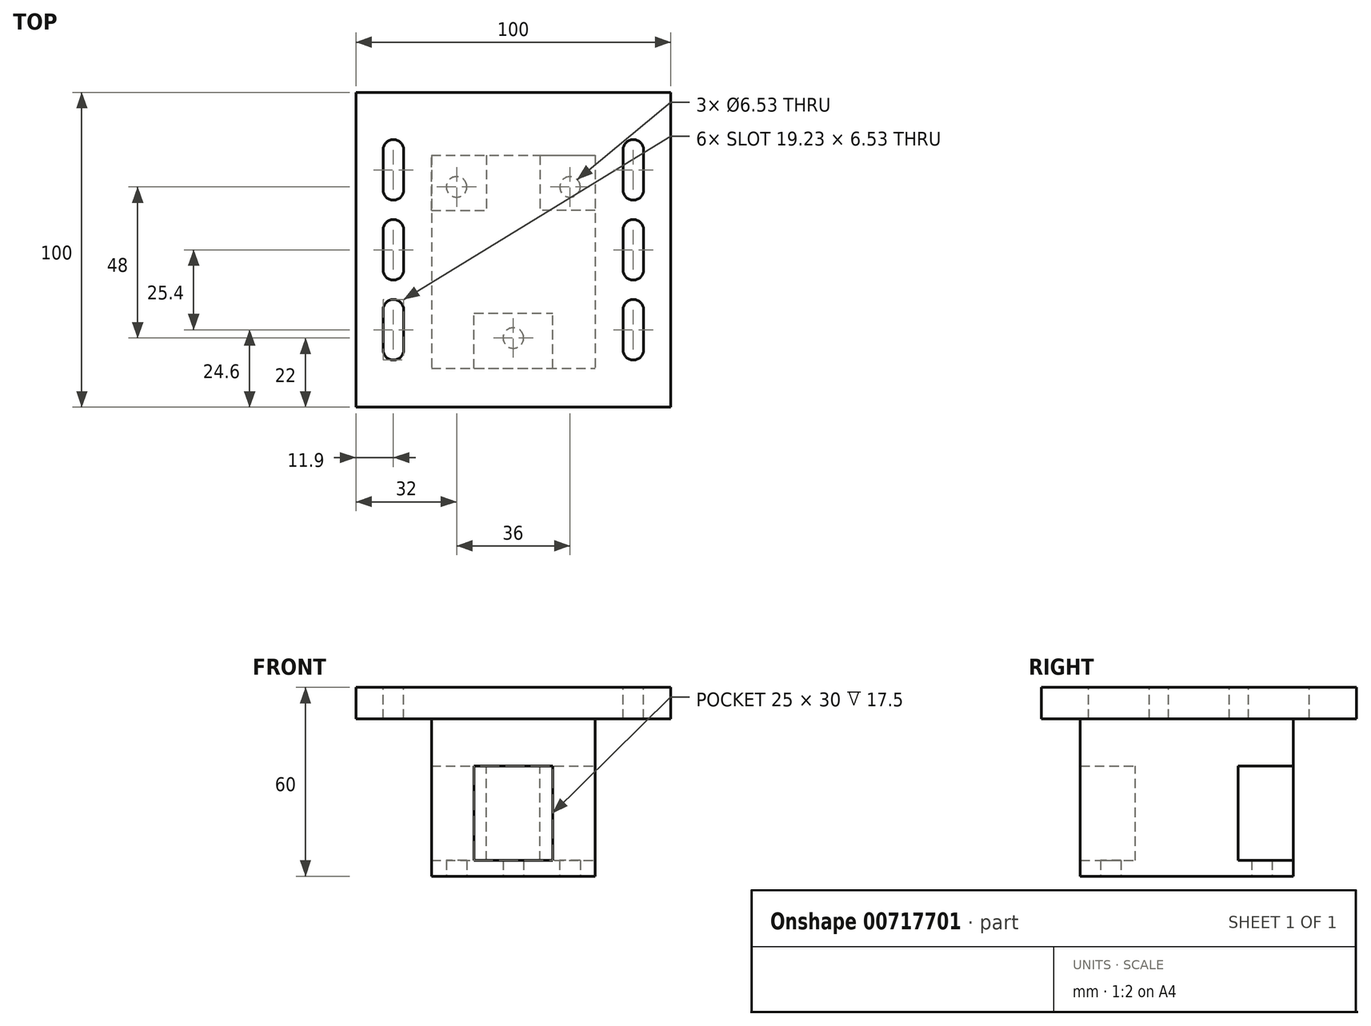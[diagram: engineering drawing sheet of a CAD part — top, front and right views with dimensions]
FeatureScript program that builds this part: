
annotation { "Feature Type Name" : "Feature", "Feature Type Description" : "" }
export const myFeature = defineFeature(function(context is Context, id is Id, definition is map)
    precondition{}
    {
        {
            var Q0;
            Q0=qCreatedBy(makeId("Top.planeOp"),FACE);
            var sketch = newSketch(context, id + "F0", { "sketchPlane" : qUnion([Q0])});
            skLineSegment(sketch, "E0.bottom", {"start": v(-26, 30) * mm, "end": v(26, 30) * mm});
            skLineSegment(sketch, "E0.top", {"start": v(-26, -37.66) * mm, "end": v(26, -37.66) * mm});
            skLineSegment(sketch, "E0.left", {"start": v(-26, 30) * mm, "end": v(-26, -37.66) * mm});
            skLineSegment(sketch, "E0.right", {"start": v(26, 30) * mm, "end": v(26, -37.66) * mm});
            skSolve(sketch);
        }
        {
            var Q0;
            Q0=makeQuery(id+"F0.imprint","IMPRINT",FACE,{"disambiguationData":[TD([[makeQuery(id+"F0.imprint","IMPRINT",EDGE,{"derivedFrom":sQuery(id+"F0.wireOp",EDGE,"E0.bottom")}),-1.0]])]});
            var sketch = newSketch(context, id + "F1", { "sketchPlane" : qUnion([Q0])});
            skCircle(sketch, "E1", {"center": v(-18, 20) * mm, "radius": 3.27 * mm});
            skCircle(sketch, "E2", {"center": v(18, 20) * mm, "radius": 3.27 * mm});
            skCircle(sketch, "E3", {"center": v(0, -28) * mm, "radius": 3.27 * mm});
            skSolve(sketch);
        }
        {
            var Q0;
            Q0 = qSketchRegion(id + "F0", true);
            extrude(context, id + "F2", {"entities" : qUnion([Q0]), "depth" : 5 * mm, "offsetDistance" : 25 * mm});
        }
        {
            var Q0;
            Q0 = qSketchRegion(id + "F1", true);
            extrude(context, id + "F3", {"entities" : qUnion([Q0]), "operationType" : NewBodyOperationType.REMOVE, "oppositeDirection" : true, "depth" : -5 * mm, "offsetDistance" : 25 * mm});
        }
        {
            var Q0;
            Q0=makeQuery(id+"F2.opExtrude","CAP_FACE",FACE,{"disambiguationData":[OSD([sQuery(id+"F0.wireOp",EDGE,"E0.bottom"),sQuery(id+"F0.wireOp",EDGE,"E0.top"),sQuery(id+"F0.wireOp",EDGE,"E0.left"),sQuery(id+"F0.wireOp",EDGE,"E0.right")])],"isStart":false});
            var sketch = newSketch(context, id + "F4", { "sketchPlane" : qUnion([Q0])});
            skLineSegment(sketch, "E4.bottom", {"start": v(-26, 30) * mm, "end": v(26, 30) * mm});
            skLineSegment(sketch, "E4.top", {"start": v(-26, -37.66) * mm, "end": v(26, -37.66) * mm});
            skLineSegment(sketch, "E4.left", {"start": v(-26, 30) * mm, "end": v(-26, -37.66) * mm});
            skLineSegment(sketch, "E4.right", {"start": v(26, 30) * mm, "end": v(26, -37.66) * mm});
            skSolve(sketch);
        }
        {
            var Q0;
            Q0 = qSketchRegion(id + "F4", true);
            extrude(context, id + "F5", {"entities" : qUnion([Q0]), "operationType" : NewBodyOperationType.ADD, "depth" : 30 * mm, "offsetDistance" : 25 * mm});
        }
        {
            var Q0;
            Q0=makeQuery(id+"F5.opExtrude","CAP_FACE",FACE,{"disambiguationData":[OSD([sQuery(id+"F4.wireOp",EDGE,"E4.bottom"),sQuery(id+"F4.wireOp",EDGE,"E4.top"),sQuery(id+"F4.wireOp",EDGE,"E4.left"),sQuery(id+"F4.wireOp",EDGE,"E4.right")])],"isStart":false});
            var sketch = newSketch(context, id + "F6", { "sketchPlane" : qUnion([Q0])});
            skLineSegment(sketch, "E5.bottom", {"start": v(-26, 30) * mm, "end": v(-8.5, 30) * mm});
            skLineSegment(sketch, "E5.top", {"start": v(-26, 12.5) * mm, "end": v(-8.5, 12.5) * mm});
            skLineSegment(sketch, "E5.left", {"start": v(-26, 30) * mm, "end": v(-26, 12.5) * mm});
            skLineSegment(sketch, "E5.right", {"start": v(-8.5, 30) * mm, "end": v(-8.5, 12.5) * mm});
            skLineSegment(sketch, "E6.bottom", {"start": v(26, 30) * mm, "end": v(8.5, 30) * mm});
            skLineSegment(sketch, "E6.top", {"start": v(26, 12.5) * mm, "end": v(8.5, 12.5) * mm});
            skLineSegment(sketch, "E6.left", {"start": v(26, 30) * mm, "end": v(26, 12.5) * mm});
            skLineSegment(sketch, "E6.right", {"start": v(8.5, 30) * mm, "end": v(8.5, 12.5) * mm});
            skLineSegment(sketch, "E7.bottom", {"start": v(-12.5, -37.66) * mm, "end": v(12.5, -37.66) * mm});
            skLineSegment(sketch, "E7.top", {"start": v(-12.5, -20.16) * mm, "end": v(12.5, -20.16) * mm});
            skLineSegment(sketch, "E7.left", {"start": v(-12.5, -37.66) * mm, "end": v(-12.5, -20.16) * mm});
            skLineSegment(sketch, "E7.right", {"start": v(12.5, -37.66) * mm, "end": v(12.5, -20.16) * mm});
            skSolve(sketch);
        }
        {
            var Q0;
            Q0 = qSketchRegion(id + "F6", true);
            extrude(context, id + "F7", {"entities" : qUnion([Q0]), "operationType" : NewBodyOperationType.REMOVE, "oppositeDirection" : true, "depth" : 30 * mm, "offsetDistance" : 25 * mm});
        }
        {
            var Q0;
            Q0=makeQuery(id+"F5.opExtrude","CAP_FACE",FACE,{"disambiguationData":[OSD([sQuery(id+"F4.wireOp",EDGE,"E4.bottom"),sQuery(id+"F4.wireOp",EDGE,"E4.top"),sQuery(id+"F4.wireOp",EDGE,"E4.left"),sQuery(id+"F4.wireOp",EDGE,"E4.right")])],"isStart":false});
            var sketch = newSketch(context, id + "F8", { "sketchPlane" : qUnion([Q0])});
            skLineSegment(sketch, "E8.bottom", {"start": v(-26, -37.66) * mm, "end": v(26, -37.66) * mm});
            skLineSegment(sketch, "E8.top", {"start": v(-26, 30) * mm, "end": v(26, 30) * mm});
            skLineSegment(sketch, "E8.left", {"start": v(-26, -37.66) * mm, "end": v(-26, 30) * mm});
            skLineSegment(sketch, "E8.right", {"start": v(26, -37.66) * mm, "end": v(26, 30) * mm});
            skSolve(sketch);
        }
        {
            var Q0;
            Q0 = qSketchRegion(id + "F8", true);
            extrude(context, id + "F9", {"entities" : qUnion([Q0]), "operationType" : NewBodyOperationType.ADD, "depth" : 25 * mm, "offsetDistance" : 25 * mm});
        }
        {
            var Q0;
            Q0=makeQuery(id+"F9.opExtrude","CAP_FACE",FACE,{"disambiguationData":[OSD([sQuery(id+"F8.wireOp",EDGE,"E8.bottom"),sQuery(id+"F8.wireOp",EDGE,"E8.top"),sQuery(id+"F8.wireOp",EDGE,"E8.left"),sQuery(id+"F8.wireOp",EDGE,"E8.right")])],"isStart":false});
            var sketch = newSketch(context, id + "F10", { "sketchPlane" : qUnion([Q0])});
            skLineSegment(sketch, "E9.bottom", {"start": v(50, -50) * mm, "end": v(-50, -50) * mm});
            skLineSegment(sketch, "E9.top", {"start": v(50, 50) * mm, "end": v(-50, 50) * mm});
            skLineSegment(sketch, "E9.left", {"start": v(50, -50) * mm, "end": v(50, 50) * mm});
            skLineSegment(sketch, "E9.right", {"start": v(-50, -50) * mm, "end": v(-50, 50) * mm});
            skPoint(sketch, "E9.middle", {"position": v(0, 0) * mm});
            skSolve(sketch);
        }
        {
            var Q0;
            Q0 = qSketchRegion(id + "F10", true);
            extrude(context, id + "F11", {"entities" : qUnion([Q0]), "operationType" : NewBodyOperationType.ADD, "oppositeDirection" : true, "depth" : 10 * mm, "offsetDistance" : 25 * mm});
        }
        {
            var Q0;
            Q0=makeQuery(id+"F11.boolean.opBoolean","MERGE",FACE,{"derivedFrom":[makeQuery(id+"F9.opExtrude","CAP_FACE",FACE,{"disambiguationData":[OSD([sQuery(id+"F8.wireOp",EDGE,"E8.bottom"),sQuery(id+"F8.wireOp",EDGE,"E8.top"),sQuery(id+"F8.wireOp",EDGE,"E8.left"),sQuery(id+"F8.wireOp",EDGE,"E8.right")])],"isStart":false}),makeQuery(id+"F11.opExtrude","CAP_FACE",FACE,{"disambiguationData":[OSD([sQuery(id+"F10.wireOp",EDGE,"E9.bottom"),sQuery(id+"F10.wireOp",EDGE,"E9.top"),sQuery(id+"F10.wireOp",EDGE,"E9.left"),sQuery(id+"F10.wireOp",EDGE,"E9.right")])],"isStart":true})]});
            var sketch = newSketch(context, id + "F12", { "sketchPlane" : qUnion([Q0])});
            skCircle(sketch, "E10", {"center": v(38.1, -6.35) * mm, "radius": 3.27 * mm});
            skCircle(sketch, "E11", {"center": v(38.1, 6.35) * mm, "radius": 3.27 * mm});
            skLineSegment(sketch, "E12.bottom", {"start": v(34.84, 6.35) * mm, "end": v(41.37, 6.35) * mm});
            skLineSegment(sketch, "E12.top", {"start": v(34.84, -6.35) * mm, "end": v(41.37, -6.35) * mm});
            skLineSegment(sketch, "E12.left", {"start": v(34.84, 6.35) * mm, "end": v(34.84, -6.35) * mm});
            skLineSegment(sketch, "E12.right", {"start": v(41.37, 6.35) * mm, "end": v(41.37, -6.35) * mm});
            skCircle(sketch, "E13", {"center": v(38.1, -31.75) * mm, "radius": 3.27 * mm});
            skCircle(sketch, "E14", {"center": v(38.1, -19.05) * mm, "radius": 3.27 * mm});
            skLineSegment(sketch, "E15.bottom", {"start": v(34.84, -19.05) * mm, "end": v(41.37, -19.05) * mm});
            skLineSegment(sketch, "E15.top", {"start": v(34.84, -31.75) * mm, "end": v(41.37, -31.75) * mm});
            skLineSegment(sketch, "E15.left", {"start": v(34.84, -19.05) * mm, "end": v(34.84, -31.75) * mm});
            skLineSegment(sketch, "E15.right", {"start": v(41.37, -19.05) * mm, "end": v(41.37, -31.75) * mm});
            skCircle(sketch, "E16.MirrorC", {"center": v(38.1, 31.75) * mm, "radius": 3.27 * mm});
            skLineSegment(sketch, "E17.MirrorCS", {"start": v(41.37, 19.05) * mm, "end": v(41.37, 31.75) * mm});
            skLineSegment(sketch, "E18.MirrorCS", {"start": v(34.84, 19.05) * mm, "end": v(34.84, 31.75) * mm});
            skCircle(sketch, "E19.MirrorC", {"center": v(38.1, 19.05) * mm, "radius": 3.27 * mm});
            skCircle(sketch, "E20.MirrorC", {"center": v(-38.1, -31.75) * mm, "radius": 3.27 * mm});
            skLineSegment(sketch, "E21.MirrorCS", {"start": v(-41.37, -19.05) * mm, "end": v(-41.37, -31.75) * mm});
            skLineSegment(sketch, "E22.MirrorCS", {"start": v(-34.84, -19.05) * mm, "end": v(-34.84, -31.75) * mm});
            skCircle(sketch, "E23.MirrorC", {"center": v(-38.1, -19.05) * mm, "radius": 3.27 * mm});
            skCircle(sketch, "E24.MirrorC", {"center": v(-38.1, -6.35) * mm, "radius": 3.27 * mm});
            skLineSegment(sketch, "E25.MirrorCS", {"start": v(-41.37, 6.35) * mm, "end": v(-41.37, -6.35) * mm});
            skLineSegment(sketch, "E26.MirrorCS", {"start": v(-34.84, 6.35) * mm, "end": v(-34.84, -6.35) * mm});
            skCircle(sketch, "E27.MirrorC", {"center": v(-38.1, 6.35) * mm, "radius": 3.27 * mm});
            skCircle(sketch, "E28.MirrorC", {"center": v(-38.1, 19.05) * mm, "radius": 3.27 * mm});
            skLineSegment(sketch, "E29.MirrorCS", {"start": v(-34.84, 19.05) * mm, "end": v(-34.84, 31.75) * mm});
            skLineSegment(sketch, "E30.MirrorCS", {"start": v(-41.37, 19.05) * mm, "end": v(-41.37, 31.75) * mm});
            skCircle(sketch, "E31.MirrorC", {"center": v(-38.1, 31.75) * mm, "radius": 3.27 * mm});
            skSolve(sketch);
        }
        {
            var Q0;
            Q0 = qSketchRegion(id + "F12", true);
            extrude(context, id + "F13", {"entities" : qUnion([Q0]), "operationType" : NewBodyOperationType.REMOVE, "oppositeDirection" : true, "depth" : 10 * mm, "offsetDistance" : 25 * mm});
        }
    });
